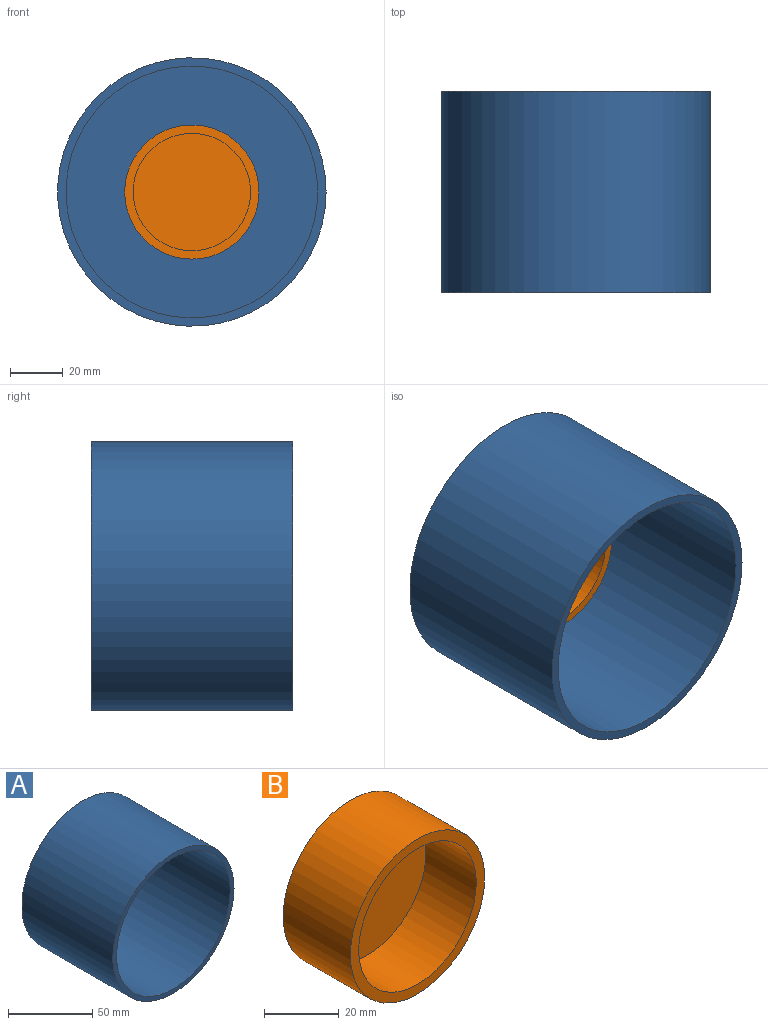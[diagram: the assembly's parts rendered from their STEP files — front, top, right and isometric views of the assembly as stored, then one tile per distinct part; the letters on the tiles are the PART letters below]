
ASSEMBLY  parts=2 mates=1
PART A: 5 faces, bbox 101.6x76.2x101.6 mm
  f0: cylinder r=47.62mm len=95.25mm, axis (0,1,0), area 20901.7mm2, adj f2,f4
  f1: cylinder r=50.8mm len=101.6mm, axis (0,1,0), area 24322mm2, adj f2,f3
  f2: plane 101.6x101.6mm, normal (0,-1,0), area 981.7mm2, adj f0,f1
  f3: plane 101.6x101.6mm, normal (0,1,0), area 8107.3mm2, adj f1
  f4: plane 95.25x95.25mm, normal (0,-1,0), area 7125.6mm2, adj f0
PART B: 5 faces, bbox 50.8x25.4x50.8 mm
  f0: cylinder r=22.23mm len=44.45mm, axis (0,1,0), area 2660.2mm2, adj f2,f4
  f1: cylinder r=25.4mm len=50.8mm, axis (0,1,0), area 4053.7mm2, adj f2,f3
  f2: plane 50.8x50.8mm, normal (0,-1,0), area 475mm2, adj f0,f1
  f3: plane 50.8x50.8mm, normal (0,1,0), area 2026.8mm2, adj f1
  f4: plane 44.45x44.45mm, normal (0,-1,0), area 1551.8mm2, adj f0
PLACE A t=(85.6,0,0)mm
PLACE B rot(axis=(0,1,0),90deg) t=(73.03,-6.35,-115.37)mm
MATE slider B.f0 <-> A.f0  axis (0,1,0) through (85.6,-6.35,0)mm
